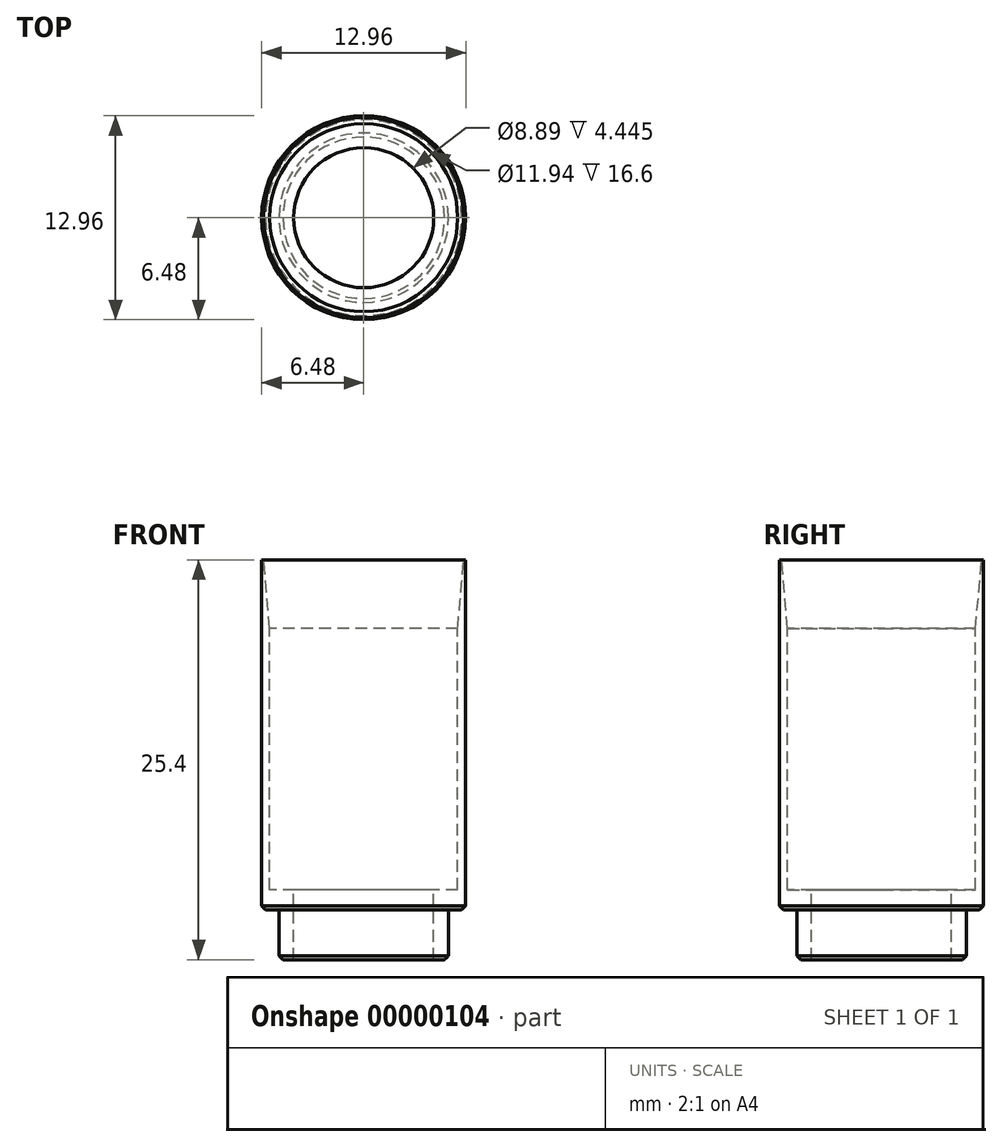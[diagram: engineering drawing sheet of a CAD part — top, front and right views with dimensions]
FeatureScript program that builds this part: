
annotation { "Feature Type Name" : "Feature", "Feature Type Description" : "" }
export const myFeature = defineFeature(function(context is Context, id is Id, definition is map)
    precondition{}
    {
        {
            var Q0;
            Q0=qCreatedBy(makeId("Front.planeOp"),FACE);
            var sketch = newSketch(context, id + "F0", { "sketchPlane" : qUnion([Q0])});
            skLineSegment(sketch, "E0", {"start": v(0, 25.4) * mm, "end": v(0, 0) * mm, "construction": true});
            skLineSegment(sketch, "E1", {"start": v(4.45, 0) * mm, "end": v(5.38, 0) * mm});
            skLineSegment(sketch, "E2", {"start": v(5.38, 0) * mm, "end": v(5.38, 3.17) * mm});
            skLineSegment(sketch, "E3", {"start": v(5.38, 3.17) * mm, "end": v(6.48, 3.18) * mm});
            skLineSegment(sketch, "E4", {"start": v(6.48, 3.18) * mm, "end": v(6.48, 25.4) * mm});
            skLineSegment(sketch, "E5", {"start": v(6.48, 25.4) * mm, "end": v(6.35, 25.4) * mm});
            skLineSegment(sketch, "E6", {"start": v(6.35, 25.4) * mm, "end": v(5.97, 21.05) * mm});
            skLineSegment(sketch, "E7", {"start": v(5.97, 21.05) * mm, "end": v(5.97, 4.45) * mm});
            skLineSegment(sketch, "E8", {"start": v(5.97, 4.45) * mm, "end": v(4.44, 4.45) * mm});
            skLineSegment(sketch, "E9", {"start": v(4.45, 4.45) * mm, "end": v(4.45, 0) * mm});
            skSolve(sketch);
        }
        {
            var Q0;
            Q0=makeQuery(id+"F0.imprint","IMPRINT",FACE,{"disambiguationData":[TD([[makeQuery(id+"F0.imprint","IMPRINT",EDGE,{"derivedFrom":sQuery(id+"F0.wireOp",EDGE,"E1")}),1.0]])]});
            var Q1;
            Q1=sQuery(id+"F0.wireOp",EDGE,"E0");
            revolve(context, id + "F1", {"entities" : qUnion([Q0]), "axis" : qUnion([Q1]), "revolveType" : RevolveType.FULL});
        }
        {
            var Q0;
            Q0=makeQuery(id+"F1.opRevolve","SWEPT_EDGE",EDGE,{"disambiguationData":[OSD([sQuery(id+"F0.wireOp",EDGE,"E1"),sQuery(id+"F0.wireOp",EDGE,"E2")])]});
            var Q1;
            Q1=makeQuery(id+"F1.opRevolve","SWEPT_EDGE",EDGE,{"disambiguationData":[OSD([sQuery(id+"F0.wireOp",EDGE,"E3"),sQuery(id+"F0.wireOp",EDGE,"E4")])]});
            chamfer(context, id + "F2", {"entities" : qUnion([Q0, Q1]), "width" : 0.25 * mm, "tangentPropagation" : true});
        }
    });
